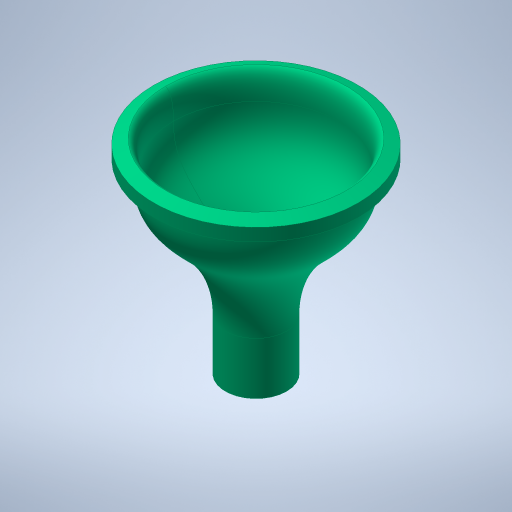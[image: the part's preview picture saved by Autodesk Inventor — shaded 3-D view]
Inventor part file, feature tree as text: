
AUTODESK INVENTOR PART (.ipt)
format: ipt  version: 2023.3 (Build 273359000, 359)  size: 585,216 bytes
history: native  units: mm
features: other x6, sketch x3, surface_op x3, revolve x1, plane x1
ambient origin geometry x8: Origin, YZ Plane, XZ Plane, XY Plane, X Axis, Y Axis, Z Axis, Center Point
bodies: Solid1 (feature_tree)
feature tree (14):
  sketch  "Sketch1"  dims[d3=7.5mm d5=5.0mm]
  revolve  "Revolution1"  [1 undecoded]
  other  "Work Axis1"
  plane  "Work Plane1"
  surface_op  "Stitch Surface2"
  sketch  "Sketch2"  dims[d6=17.453293mm]
  other  "Srf7"
  other  "Srf8"
  sketch  "Sketch4"  dims[d8=360.0deg d29=31.0mm d32=10.5mm d34=2.0mm d35=0.845184mm d36=2.0mm d42=2.0mm d48=15.0mm d52=0.5mm d53=0.5mm d54=45.0deg d55=1.0mm d58=0.0mm d59=0.0mm d60=5.0mm d61=0.0mm d62=5.0mm d63=0.0mm d64=26.0mm]
  other  "Srf9"
  other  "Srf10"
  other  "OffsetSrf2"
  surface_op  "Boundary Patch5"
  surface_op  "Boundary Patch6"
note: 1 required parameter value undecoded (feature->parameter linkage not recoverable at this tier; creation-order binding heuristic only, values carry confidence <= 0.55)
